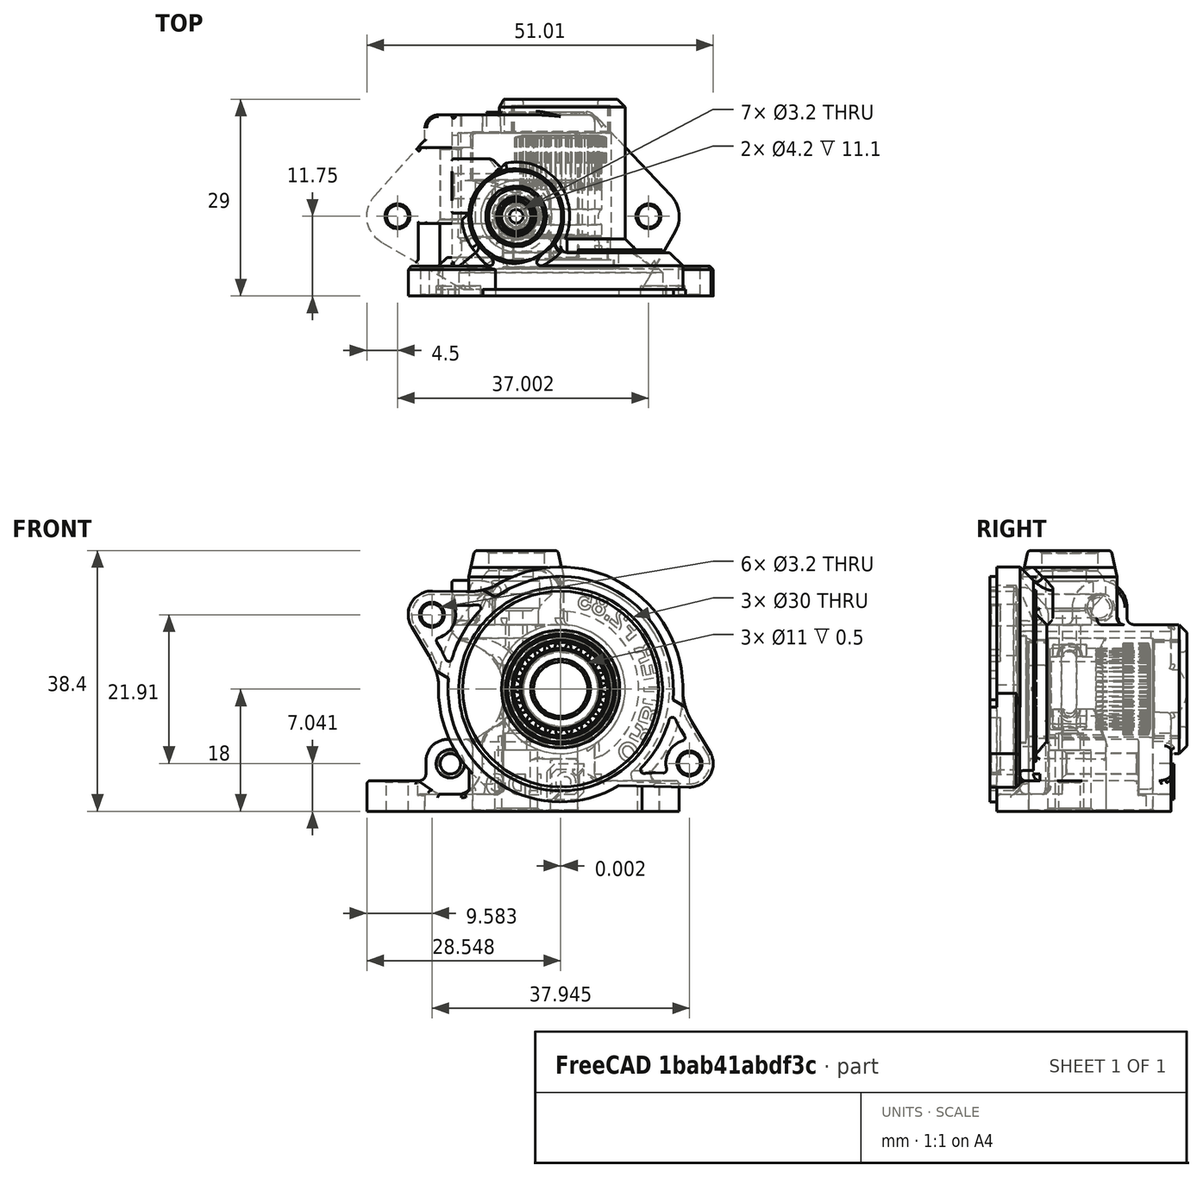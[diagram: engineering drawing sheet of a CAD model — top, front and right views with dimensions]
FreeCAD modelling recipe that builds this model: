
FCSTD DOCUMENT  (FreeCAD 0.19R24291 (Git))
Label: orbitor285-110
License: Other
LicenseURL: GPL3
objects: Part::Cylinder×15, Part::Cut×11, Part::Feature×7, Part::MultiFuse×4, Part::Box×3, Part::MultiCommon×3, Part::Chamfer×3, Part::Extrusion×1, Part::Refine×1
note: 48 computed .brp shape members not serialized (recipe doc carries the construction recipe); baked Part::Feature solids carry a one-line shape summary decoded from their .brp

FEATURE [Part::Feature] Part__Feature085001  label="base-body"
  Placement = pos=(6.54815,-12.75,18) rot=(0,0,1;0rad)
  shape: bbox 135.7 x 30.33 x 139 mm, 688 faces (baked)
FEATURE [Part::Feature] Part__Feature085004  label="MotorGear002"
  Placement = pos=(13.0949,0,0) rot=(0,0,1;0rad)
  shape: bbox 14.64 x 15 x 14.64 mm, 359 faces (baked)
FEATURE [Part::Feature] Part__Feature085003_cs
  shape: bbox 44.11 x 1e-05 x 38.4 mm, 0 faces, 0 solids (baked)
FEATURE [Part::Extrusion] Extrude
  Base = -> Part__Feature085003_cs
  Dir = (0,1,0)
  DirMode = 2
  FaceMakerClass = Part::FaceMakerBullseye
  LengthFwd = 10
  LengthRev = 0
  Placement = pos=(0,-8,0) rot=(0,0,1;0rad)
  Solid = true
  Symmetric = false
FEATURE [Part::Box] Box  label="Cube"
  AttacherType = Attacher::AttachEngine3D
  Height = 10
  Length = 5
  Placement = pos=(-2.5,-2.5,11) rot=(0,0,1;0rad)
  Width = 5
FEATURE [Part::Box] Box001  label="Cube001"
  AttacherType = Attacher::AttachEngine3D
  Height = 4
  Length = 5
  Placement = pos=(-2.5,-2.5,22) rot=(0,0,1;0rad)
  Width = 5
FEATURE [Part::Feature] Extrude001
  Placement = pos=(0,-8,0) rot=(0,0,1;0rad)
  shape: bbox 44.13 x 10.02 x 38.42 mm, 83 faces (baked)
FEATURE [Part::MultiCommon] Common
  Shapes = -> [Extrude,Box]
FEATURE [Part::MultiCommon] Common001
  Shapes = -> [Extrude001,Box001]
FEATURE [Part::Cylinder] Cylinder
  Angle = 360
  AttacherType = Attacher::AttachEngine3D
  Height = 11.1
  Radius = 4
FEATURE [Part::Cylinder] Cylinder001
  Angle = 360
  AttacherType = Attacher::AttachEngine3D
  Height = 2.1
  Placement = pos=(0,0,25.9) rot=(0,0,1;0rad)
  Radius = 2.7
FEATURE [Part::Feature] Cut004002001  label="Cut004003"
  Placement = pos=(-4.3,5.99999,-1e-15) rot=(1,0,0;1.5708rad)
  shape: bbox 7.2 x 7.2 x 10.34 mm, 15 faces, 2 solids (baked)
FEATURE [Part::Cylinder] Cylinder002
  Angle = 360
  AttacherType = Attacher::AttachEngine3D
  Height = 10
  Placement = pos=(2,-4.1,1.7) rot=(0,0,1;0rad)
  Radius = 2
FEATURE [Part::Cut] Cut
  Base = -> Cut004002001
  Placement = pos=(0,0,18.1) rot=(0,0,1;0rad)
  Tool = -> Cylinder002
FEATURE [Part::Cylinder] Cylinder004
  Angle = 360
  AttacherType = Attacher::AttachEngine3D
  Height = 2.1
  Placement = pos=(0,0,27.3) rot=(0,0,1;0rad)
  Radius = 3.3
FEATURE [Part::Cylinder] Cylinder005
  Angle = 360
  AttacherType = Attacher::AttachEngine3D
  Height = 9.1
  Placement = pos=(0,0,29.3) rot=(0,0,1;0rad)
  Radius = 5.3
FEATURE [Part::MultiFuse] Fusion003
  Shapes = -> [Cylinder005,Cylinder004,Cylinder001]
FEATURE [Part::Cylinder] Cylinder006
  Angle = 360
  AttacherType = Attacher::AttachEngine3D
  Height = 10
  Placement = pos=(-13.1,4.4,30) rot=(0,1,0;1.5708rad)
  Radius = 2
FEATURE [Part::Cut] Cut004002002
  Base = -> Fusion003
  Tool = -> Cylinder006
FEATURE [Part::Cylinder] Cylinder007
  Angle = 360
  AttacherType = Attacher::AttachEngine3D
  Height = 10
  Placement = pos=(0,0,35.9) rot=(0,0,1;0rad)
  Radius = 8
FEATURE [Part::Cylinder] Cylinder008
  Angle = 360
  AttacherType = Attacher::AttachEngine3D
  Height = 39
  Radius = 1
FEATURE [Part::Cylinder] Cylinder009
  Angle = 360
  AttacherType = Attacher::AttachEngine3D
  Height = 11.5
  Radius = 2.1
FEATURE [Part::Feature] Part__Feature082001001  label="new-housing"
  Placement = pos=(6.55,-12.75,18) rot=(0,0,1;0rad)
  shape: bbox 135.7 x 30.34 x 139 mm, 687 faces (baked)
FEATURE [Part::MultiFuse] Fusion
  Shapes = -> [Part__Feature082001001,Cylinder,Common001,Common]
FEATURE [Part::Cut] Cut004002003
  Base = -> Fusion
  Tool = -> Cylinder009
FEATURE [Part::MultiFuse] Fusion004
  Shapes = -> [Cut004002003,Cut004002002]
FEATURE [Part::Cut] Cut004002004
  Base = -> Fusion004
  Tool = -> Cylinder008
FEATURE [Part::Cut] Cut004002005
  Base = -> Cut004002004
  Tool = -> Cylinder007
FEATURE [Part::Cut] Cut004002006
  Base = -> Cut004002005
  Tool = -> Cut
FEATURE [Part::Chamfer] Chamfer
  Base = -> Cut004002006
  Edges = 2 edges r=0.4: [Edge817,Edge1084]
FEATURE [Part::Refine] Chamfer001
  Source = -> Chamfer
FEATURE [Part::Feature] Chamfer001001  label="orbitor-v2-mbdy"
  shape: bbox 135.7 x 30.34 x 139 mm, 715 faces (baked)
FEATURE [Part::Cylinder] Cylinder010
  Angle = 360
  AttacherType = Attacher::AttachEngine3D
  Height = 10
  Placement = pos=(6.55,-3.1,18) rot=(1,0,0;1.5708rad)
  Radius = 7.26
FEATURE [Part::Cylinder] Cylinder011
  Angle = 360
  AttacherType = Attacher::AttachEngine3D
  Height = 6
  Placement = pos=(6.55,16.25,18) rot=(1,0,0;1.5708rad)
  Radius = 7.26
FEATURE [Part::Cylinder] Cylinder012
  Angle = 360
  AttacherType = Attacher::AttachEngine3D
  Height = 10
  Placement = pos=(6.55,-5.4,18) rot=(1,0,0;1.5708rad)
  Radius = 8.5
FEATURE [Part::Box] Box002  label="Cube002"
  AttacherType = Attacher::AttachEngine3D
  Height = 10
  Length = 17
  Placement = pos=(-6,14.95,-3) rot=(0,0,1;0rad)
  Width = 10
FEATURE [Part::Cylinder] Cylinder013
  Angle = 360
  AttacherType = Attacher::AttachEngine3D
  Height = 10
  Placement = pos=(6.55,-3.1,18) rot=(1,0,0;1.5708rad)
  Radius = 16.1
FEATURE [Part::Cylinder] Cylinder014
  Angle = 360
  AttacherType = Attacher::AttachEngine3D
  Height = 10
  Placement = pos=(6.55,-3.1,18) rot=(1,0,0;1.5708rad)
  Radius = 12.1
FEATURE [Part::Cut] Cut004002009
  Base = -> Cylinder013
  Placement = pos=(0,7.75,0) rot=(0,0,1;0rad)
  Tool = -> Cylinder014
FEATURE [Part::Cylinder] Cylinder015
  Angle = 52
  AttacherType = Attacher::AttachEngine3D
  Height = 20
  Placement = pos=(6.55,7.6,18) rot=(-0.930961,0.258178,-0.258178;4.64091rad)
  Radius = 23.1
FEATURE [Part::MultiCommon] Common002
  Shapes = -> [Cylinder015,Cut004002009]
FEATURE [Part::MultiFuse] Fusion005
  Shapes = -> [Cylinder010,Cylinder011]
FEATURE [Part::Cut] Cut004002010
  Base = -> Chamfer001
  Tool = -> Fusion005
FEATURE [Part::Cut] Cut004002011
  Base = -> Cut004002010
  Tool = -> Cylinder012
FEATURE [Part::Cut] Cut004002012
  Base = -> Cut004002011
  Tool = -> Box002
FEATURE [Part::Cut] Cut004002013
  Base = -> Cut004002012
  Tool = -> Common002
FEATURE [Part::Chamfer] Chamfer001002
  Base = -> Cut004002013
  Edges = 1 edges r=0.2: [Edge238]
FEATURE [Part::Chamfer] Chamfer001003
  Base = -> Chamfer001002
  Edges = 2 edges r=0.2: [Edge387,Edge994]
